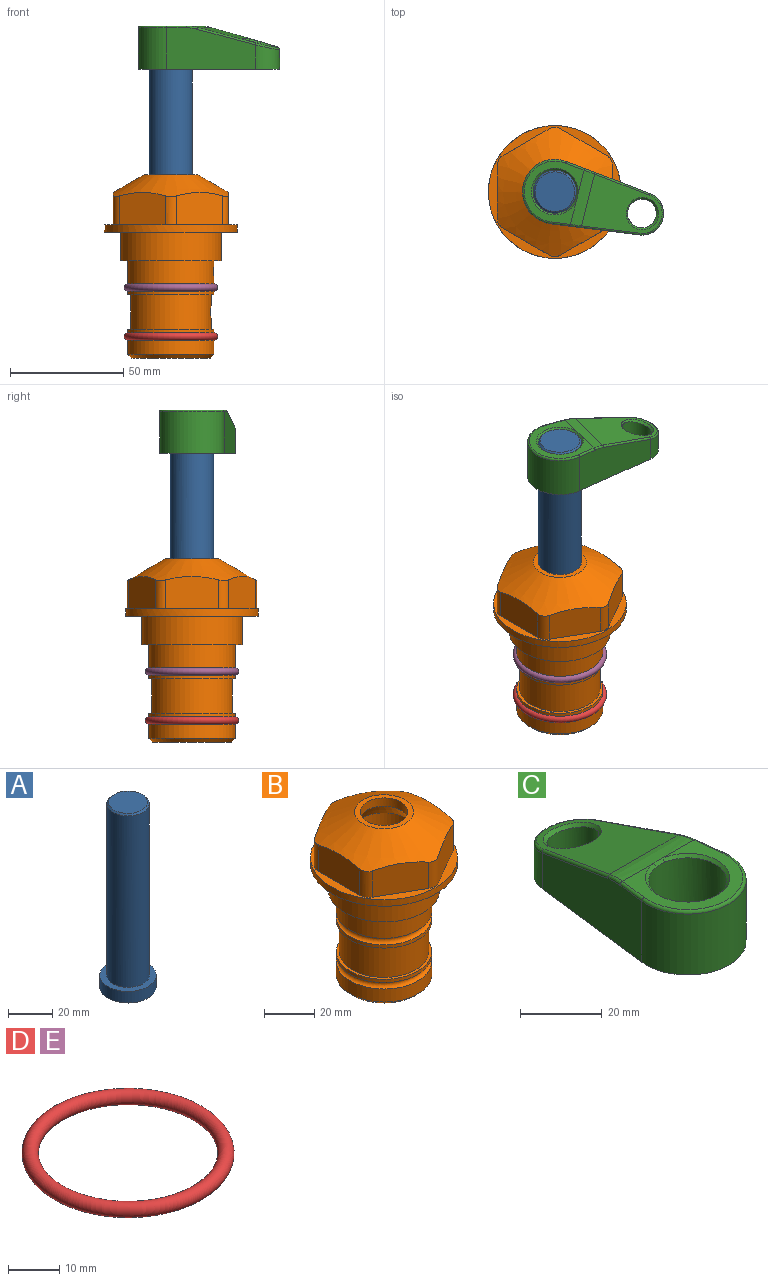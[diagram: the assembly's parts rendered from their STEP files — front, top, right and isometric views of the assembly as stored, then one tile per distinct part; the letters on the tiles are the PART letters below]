
ASSEMBLY  parts=5 mates=4
PART A: 6 faces, bbox 25.4x25.4x101.6 mm
  f0: plane 17.46x17.46mm, normal (0,0,1), area 239.5mm2, adj f5
  f1: plane 25.4x25.4mm, normal (0,0,-1), area 506.7mm2, adj f2
  f2: cylinder r=12.7mm len=25.4mm, axis (0,0,1), area 506.7mm2, adj f1,f3
  f3: plane 25.4x25.4mm, normal (0,0,1), area 221.7mm2, adj f2,f4
  f4: cylinder r=9.53mm len=94.46mm, axis (0,0,1), area 5653mm2, adj f3,f5
  f5: cone r=8.73mm half-angle=45deg, axis (0,0,-1), area 64.4mm2, adj f0,f4
PART B: 36 faces, bbox 58.7x58.7x81 mm
  f0: cylinder r=17.78mm len=35.56mm, axis (0,0,1), area 1670.8mm2, adj f23,f24,f31
  f1: cylinder r=19.05mm len=38.1mm, axis (0,0,1), area 1191.9mm2, adj f26,f27,f30
  f2: plane 58.66x58.66mm, normal (0,0,-1), area 1150.6mm2, adj f3,f28
  f3: cylinder r=29.33mm len=58.66mm, axis (0,0,-1), area 585.1mm2, adj f2,f4
  f4: plane 58.66x58.66mm, normal (0,0,1), area 475.9mm2, adj f3,f5,f6,f7,f8,f9,f10,f11
  f5: plane 20.32x14.34mm, normal (-0.5,0.87,0), area 324.4mm2, adj f4,f15,f16,f17
  f6: plane 20.32x14.34mm, normal (0.5,0.87,0), area 324.4mm2, adj f4,f14,f15,f17
  f7: plane 23.48x14.34mm, normal (1,0,0), area 324.4mm2, adj f4,f13,f14,f17
  f8: plane 20.32x14.34mm, normal (0.5,-0.87,0), area 324.4mm2, adj f4,f12,f13,f17
  f9: plane 20.32x14.34mm, normal (-0.5,-0.87,0), area 324.4mm2, adj f4,f11,f12,f17
  f10: plane 23.48x14.34mm, normal (-1,0,0), area 324.4mm2, adj f4,f11,f16,f17
  f11: cylinder r=5.08mm len=12.85mm, axis (0,0,-1), area 67.2mm2, adj f4,f9,f10,f17
  f12: cylinder r=5.08mm len=12.85mm, axis (0,0,-1), area 67.2mm2, adj f4,f8,f9,f17
  f13: cylinder r=5.08mm len=12.85mm, axis (0,0,-1), area 67.2mm2, adj f4,f7,f8,f17
  f14: cylinder r=5.08mm len=12.85mm, axis (0,0,-1), area 67.2mm2, adj f4,f6,f7,f17
  f15: cylinder r=5.08mm len=12.85mm, axis (0,0,-1), area 67.2mm2, adj f4,f5,f6,f17
  f16: cylinder r=5.08mm len=12.85mm, axis (0,0,-1), area 67.2mm2, adj f4,f5,f10,f17
  f17: cone r=11.73mm half-angle=60deg, axis (0,0,-1), area 2071.8mm2, adj f5,f6,f7,f8,f9,f10,f11,f12
  f18: plane 23.46x23.46mm, normal (0,0,1), area 147.4mm2, adj f17,f35
  f19: plane 34.93x34.93mm, normal (0,0,-1), area 958mm2, adj f29
  f20: cylinder r=19.05mm len=38.1mm, axis (0,0,1), area 760.1mm2, adj f21,f29
  f21: torus R=19.05mm, axis (0,0,1), area 565.3mm2, adj f20,f22
  f22: cylinder r=19.05mm len=38.1mm, axis (0,0,1), area 190mm2, adj f21,f23
  f23: plane 38.1x38.1mm, normal (0,0,1), area 146.9mm2, adj f0,f22
  f24: plane 38.1x38.1mm, normal (0,0,-1), area 146.9mm2, adj f0,f25
  f25: cylinder r=19.05mm len=38.1mm, axis (0,0,1), area 190mm2, adj f24,f26
  f26: torus R=19.05mm, axis (0,0,1), area 565.3mm2, adj f1,f25
  f27: plane 44.45x44.45mm, normal (0,0,-1), area 411.7mm2, adj f1,f28
  f28: cylinder r=22.23mm len=44.45mm, axis (0,0,1), area 1773.5mm2, adj f2,f27
  f29: cone r=19.05mm half-angle=45deg, axis (0,0,1), area 257.5mm2, adj f19,f20
  f30: cylinder r=3.17mm len=6.75mm, axis (-1,0,0), area 128mm2, adj f1,f33
  f31: cylinder r=3.17mm len=6.35mm, axis (-1,0,0), area 102.5mm2, adj f0,f33
  f32: plane 25.4x25.4mm, normal (0,0,1), area 506.7mm2, adj f33
  f33: cylinder r=12.7mm len=66.42mm, axis (0,0,-1), area 5236.2mm2, adj f30,f31,f32,f34
  f34: cone r=9.53mm half-angle=30deg, axis (0,0,-1), area 443.4mm2, adj f33,f35
  f35: cylinder r=9.53mm len=19.05mm, axis (0,0,-1), area 240.9mm2, adj f18,f34
PART C: 31 faces, bbox 31.7x65.5x19.8 mm
  f0: plane 39.12x18.26mm, normal (0.99,0.12,0), area 612.2mm2, adj f1,f4,f7,f11,f13,f15
  f1: cylinder r=9.53mm len=18.91mm, axis (0,0,-1), area 296.1mm2, adj f0,f2,f7,f17
  f2: plane 39.12x18.26mm, normal (-0.99,0.12,0), area 612.2mm2, adj f1,f4,f7,f12,f14,f16
  f3: cylinder r=6.35mm len=12.7mm, axis (0,0,-1), area 362.4mm2, adj f7,f18
  f4: cylinder r=14.29mm len=28.58mm, axis (0,0,-1), area 882.2mm2, adj f0,f2,f7,f10
  f5: cylinder r=9.53mm len=19.05mm, axis (0,0,-1), area 1092.6mm2, adj f7,f19,f20
  f6: plane 26.99x23.69mm, normal (0,0,1), area 216.2mm2, adj f9,f10,f11,f12,f19
  f7: plane 63.5x28.58mm, normal (0,0,-1), area 661.8mm2, adj f0,f1,f2,f3,f4,f5,f22,f23
  f8: plane 33.52x23.6mm, normal (0,0.26,0.97), area 486mm2, adj f9,f15,f16,f17,f18
  f9: cylinder r=19.05mm len=24.72mm, axis (1,0,0), area 120.4mm2, adj f6,f8,f13,f14,f20
  f10: torus R=13.49mm, axis (0,0,1), area 59mm2, adj f4,f6,f11,f12
  f11: cylinder r=0.79mm len=8.67mm, axis (0.12,-0.99,0), area 10.8mm2, adj f0,f6,f10,f13
  f12: cylinder r=0.79mm len=8.67mm, axis (0.12,0.99,0), area 10.8mm2, adj f2,f6,f10,f14
  f13: bspline ~4.95x1.42mm, area 6.1mm2, adj f0,f9,f11,f15
  f14: bspline ~4.95x1.42mm, area 6.1mm2, adj f2,f9,f12,f16
  f15: cylinder r=0.79mm len=25.95mm, axis (0.12,-0.96,0.26), area 32.9mm2, adj f0,f8,f13,f17
  f16: cylinder r=0.79mm len=25.95mm, axis (0.12,0.96,-0.26), area 32.9mm2, adj f2,f8,f14,f17
  f17: bspline ~18.91x8.38mm, area 30mm2, adj f1,f8,f15,f16
  f18: bspline ~14.29x14.29mm, area 48.3mm2, adj f3,f8
  f19: cone r=9.53mm half-angle=45deg, axis (0,0,1), area 66.5mm2, adj f5,f6,f20
  f20: bspline ~3.22x0.96mm, area 3.5mm2, adj f5,f9,f19
  f21: plane 2.75x2.72mm, normal (0,0,-1), area 2.9mm2, adj f23,f25,f28
  f22: plane 23.05x15.88mm, normal (-0.99,-0.12,0), area 323.6mm2, adj f7,f25,f26,f27,f28,f29
  f23: plane 23.05x15.88mm, normal (0.99,-0.12,0), area 323.6mm2, adj f7,f21,f25,f27,f28,f30
  f24: cylinder r=9.53mm len=10.69mm, axis (0,0,-1), area 114.7mm2, adj f7,f27,f29,f30
  f25: cylinder r=12.7mm len=20.59mm, axis (0,0,-1), area 381.1mm2, adj f7,f21,f22,f23,f26,f28
  f26: plane 2.75x2.72mm, normal (0,0,-1), area 2.9mm2, adj f22,f25,f28
  f27: plane 19.72x18.37mm, normal (0,-0.26,-0.97), area 291.8mm2, adj f22,f23,f24,f28,f29,f30
  f28: cylinder r=15.88mm len=19.92mm, axis (1,0,0), area 54.8mm2, adj f21,f22,f23,f25,f26,f27
  f29: cylinder r=1.59mm len=11mm, axis (0,0,-1), area 34.7mm2, adj f7,f22,f24,f27
  f30: cylinder r=1.59mm len=11mm, axis (0,0,-1), area 34.7mm2, adj f7,f23,f24,f27
PART D: 1 faces, bbox 44.7x44.7x3.2 mm
  f0: torus R=19.05mm, axis (0,0,1), area 1193.9mm2
PART E: same geometry as D
PLACE A rot(axis=(0,0,-1),104.1deg) t=(0,0,27.55)mm
PLACE B at identity fixed
PLACE C rot(axis=(0,0,-1),104.1deg) t=(0,0,27.55)mm
PLACE D t=(0,0,-21.59)mm
PLACE E at identity
MATE fastened E.f0 <-> B.f0  axis (0,0,1) through (0,0,-24.51)mm
MATE fastened A.f2 <-> C.f4  axis (0,0,1) through (0,0,91.05)mm
MATE cylindrical A.f2 <-> B.f0  axis (0,0,-1) through (0,0,-10.55)mm
MATE fastened B.f0 <-> D.f0  axis (0,0,1) through (0,0,-46.1)mm
